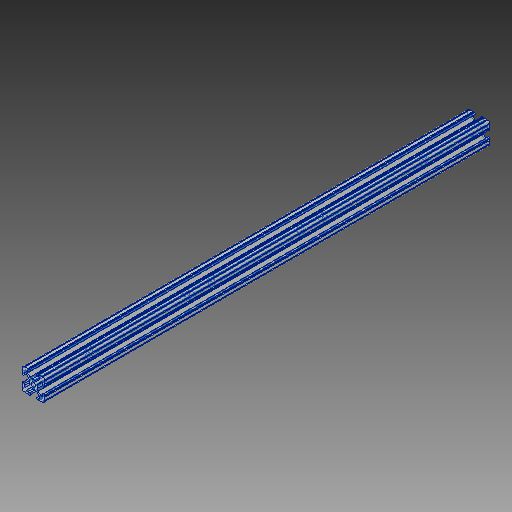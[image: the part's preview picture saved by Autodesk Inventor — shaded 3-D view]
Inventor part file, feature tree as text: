
AUTODESK INVENTOR PART (.ipt)
format: ipt  version: 2019 (Build 230136000, 136)  size: 396,288 bytes
history: native  units: in
note: dims shown in document units (in); Inventor stores cm internally (conversion verified against a paired STEP export)
features: extrude x3, sketch x3, other x1, plane x1, projected_geometry x1
ambient origin geometry x8: Origin, YZ Plane, XZ Plane, XY Plane, X Axis, Y Axis, Z Axis, Center Point
bodies: Solid1 (feature_tree)
feature tree (9):
  other  "Boss-Extrude1"
  extrude  "Extrusion1"  Depth=0.4375in
  plane  "Work Plane1"
  sketch  "Sketch6"  dims[d12=2.125in d13=0.25in]
  extrude  "Extrusion6"  Depth=0.25in
  extrude  "Extrusion7"  Depth=1.0in TaperAngle=0.0deg
  sketch  "Sketch1"  dims[d0=8.0in d1=0.0in d11=0.4375in]
  projected_geometry  "Projected Loop1"
  sketch  "Sketch7"  dims[d14=3.0in d17=1.0in d18=0.0in d19=1.0in d20=0.0in]
